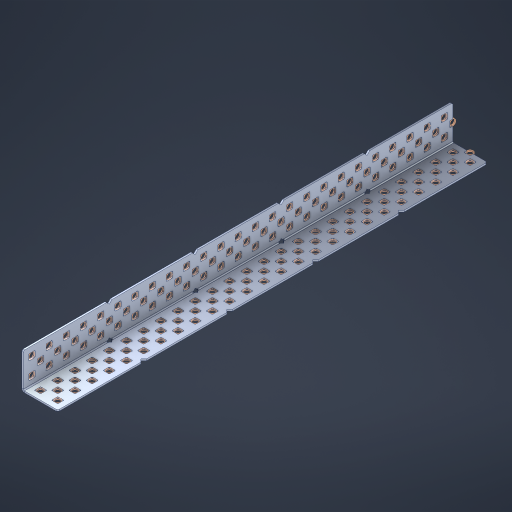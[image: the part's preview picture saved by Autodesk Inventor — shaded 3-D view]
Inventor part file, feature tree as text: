
AUTODESK INVENTOR PART (.ipt)
format: ipt  version: 2023 (Build 270158000, 158)  size: 1,781,248 bytes
history: native  units: in
note: dims shown in document units (in); Inventor stores cm internally (conversion verified against a paired STEP export)
features: other x156, extrude x148, sheet_metal_op x8, sketch x7, pattern_linear x2, mirror x1, chamfer x1
ambient origin geometry x8: Origin, YZ Plane, XZ Plane, XY Plane, X Axis, Y Axis, Z Axis, Center Point
bodies: Solid1 (feature_tree), Body (feature_tree)
feature tree (323):
  sheet_metal_op  "Flanges"
  sheet_metal_op  "Body Pattern"
  pattern_linear  "Center Pattern"  Spacing1=1.0in  [1 undecoded]
  other  "Arc Length"
  pattern_linear  "Notch Pattern"  Spacing1=0.1875in  [1 undecoded]
  other  "Diagonal Plane"
  mirror  "Everything Mirrored"
  chamfer  "End Chamfer"
  sketch  "Sketch1"  dims[d0=1.0in]
  other  "Plate1"
  sketch  "Sketch2"  dims[d1=12.5in]
  other  "Plate2"
  sheet_metal_op  "Bend1"
  sheet_metal_op  "Corner1"
  sketch  "Sketch8"  dims[d2=0.0469in]
  sketch  "Sketch9"  dims[d3=0.0469in]
  other  "Srf91"
  sheet_metal_op  "Body Pattern Sketch"
  other  "Srf92"
  sketch  "Sketch13"  dims[d4=0.0234in]
  sketch  "Sketch15"  dims[d5=0.0938in]
  sketch  "Sketch16"  dims[d6=0.0469in d7=1.0in d8=90.0deg d9=0.0312in d10=0.1875in d11=0.0469in d12=0.0469in d49=0.182in d50=0.02in d52=0.25in d53=0.0469in d54=0.0in d55=0.172in d56=1.0in d57=0.0in d60=9.8425in d62=0.5in d63=0.7874in d65=0.5in d85=0.1473in d86=0.1659in d89=0.0469in d90=0.0in d91=0.04in d92=0.0491in d95=2.5in d96=0.04in d97=0.25in d98=45.0deg d99=0.25in d106=0.182in d107=0.02in d108=0.5in d110=0.0469in d111=0.0in d112=0.172in d113=0.5in d114=0.0in d117=0.5in d123=0.25in d125=0.25in d126=0.0491in d127=0.1227in d128=0.08in d129=0.04in d130=2.5in]
  other  "Srf786"
  other  "Srf856"
  other  "Srf857"
  other  "Srf858"
  other  "Srf859"
  other  "Srf860"
  other  "Srf861"
  other  "Srf889"
  other  "Srf890"
  other  "Srf891"
  other  "Srf1275"
  other  "Srf1276"
  other  "Srf1278"
  other  "Srf1279"
  other  "Srf1280"
  other  "Srf1281"
  other  "Srf1282"
  other  "Srf1283"
  other  "Srf1277"
  other  "Srf1285"
  other  "Srf1286"
  other  "Srf1287"
  other  "Srf1383"
  other  "Srf1384"
  other  "Srf1385"
  other  "Srf1386"
  other  "Srf1387"
  other  "Srf1388"
  other  "Srf1389"
  other  "Srf1390"
  other  "Srf1391"
  other  "Srf1392"
  other  "Srf1393"
  other  "Srf1394"
  other  "Srf1395"
  other  "Srf1396"
  other  "Srf1397"
  other  "Srf1398"
  other  "Srf1399"
  other  "Srf1400"
  other  "Srf1401"
  other  "Srf1402"
  other  "Srf1403"
  other  "Srf1404"
  other  "Srf1405"
  other  "Srf1406"
  other  "Srf1407"
  other  "Srf1408"
  other  "Srf1409"
  other  "Srf1410"
  other  "Srf1411"
  other  "Srf1412"
  other  "Srf1413"
  other  "Srf1414"
  other  "Srf1415"
  other  "Srf1416"
  other  "Srf1417"
  other  "Srf1418"
  other  "Srf1419"
  other  "Srf1420"
  other  "Srf1421"
  other  "Srf1422"
  other  "Srf1423"
  other  "Srf1424"
  other  "Srf1445"
  other  "Srf1446"
  other  "Srf1447"
  other  "Srf1448"
  other  "Srf1449"
  other  "Srf1450"
  other  "Srf1451"
  other  "Srf1452"
  other  "Srf1453"
  other  "Srf1454"
  other  "Srf1455"
  other  "Srf1456"
  other  "Srf1457"
  other  "Srf1458"
  other  "Srf1459"
  other  "Srf1460"
  other  "Srf1461"
  other  "Srf1462"
  other  "Srf1463"
  other  "Srf1464"
  other  "Srf1465"
  other  "Srf1475"
  other  "Srf1476"
  other  "Srf1477"
  other  "Srf1478"
  other  "Srf1479"
  other  "Srf1480"
  other  "Srf1481"
  other  "Srf1482"
  other  "Srf1483"
  other  "Srf1484"
  other  "Srf1485"
  other  "Srf1486"
  other  "Srf1487"
  other  "Srf1488"
  other  "Srf1489"
  other  "Srf1490"
  other  "Srf1491"
  other  "Srf1492"
  other  "Srf1493"
  other  "Srf1494"
  other  "Srf1495"
  other  "Srf1496"
  other  "Srf1497"
  other  "Srf1498"
  other  "Srf1499"
  other  "Srf1500"
  other  "Srf1501"
  other  "Srf1502"
  other  "Srf1503"
  other  "Srf1504"
  other  "Srf1505"
  other  "Srf1506"
  other  "Srf1507"
  other  "Srf1508"
  other  "Srf1509"
  other  "Srf1510"
  other  "Srf1511"
  other  "Srf1512"
  other  "Srf1513"
  other  "Srf1514"
  other  "Srf1515"
  other  "Srf1516"
  other  "Srf1537"
  other  "Srf1538"
  other  "Srf1539"
  other  "Srf1540"
  other  "Srf1541"
  other  "Srf1542"
  other  "Srf1543"
  other  "Srf1544"
  other  "Srf1545"
  other  "Srf1546"
  other  "Srf1547"
  other  "Srf1548"
  other  "Srf1549"
  other  "Srf1550"
  other  "Srf1551"
  other  "Srf1552"
  other  "Srf1553"
  other  "Srf1554"
  other  "Srf1555"
  other  "Srf1556"
  other  "Srf1557"
  sheet_metal_op  "Body Stamp"
  sheet_metal_op  "Body Circle"
  other  "Center Stamp"
  other  "Center Circle"
  sheet_metal_op  "Notch"
  extrude  "ExtrusionSrf92"  Depth=0.0469in
  extrude  "ExtrusionSrf856"  Depth=0.0469in
  extrude  "ExtrusionSrf857"  Depth=0.182in
  extrude  "ExtrusionSrf858"  Depth=0.02in
  extrude  "ExtrusionSrf859"  Depth=0.25in
  extrude  "ExtrusionSrf860"  Depth=0.0469in
  extrude  "ExtrusionSrf861"  TaperAngle=0.0deg  [1 undecoded]
  extrude  "ExtrusionSrf889"  Depth=2.5in
  extrude  "ExtrusionSrf890"  Depth=1.0in TaperAngle=0.0deg
  extrude  "ExtrusionSrf891"  Depth=2.5in
  extrude  "ExtrusionSrf1275"  Depth=0.5in
  extrude  "ExtrusionSrf1276"  Depth=2.5in
  extrude  "ExtrusionSrf1277"  Depth=2.5in
  extrude  "ExtrusionSrf1278"  Depth=0.0469in
  extrude  "ExtrusionSrf1279"  Depth=2.5in TaperAngle=0.0deg
  extrude  "ExtrusionSrf1280"  Depth=2.5in
  extrude  "ExtrusionSrf1281"  Depth=0.25in TaperAngle=45.0deg
  extrude  "ExtrusionSrf1282"  Depth=0.25in
  extrude  "ExtrusionSrf1345"  Depth=0.182in
  extrude  "ExtrusionSrf1346"  Depth=0.02in
  extrude  "ExtrusionSrf1347"  Depth=0.5in
  extrude  "ExtrusionSrf1348"  Depth=0.0469in
  extrude  "ExtrusionSrf1383"  TaperAngle=0.0deg  [1 undecoded]
  extrude  "ExtrusionSrf1384"  Depth=2.5in
  extrude  "ExtrusionSrf1385"  Depth=0.5in TaperAngle=0.0deg
  extrude  "ExtrusionSrf1386"  Depth=0.5in
  extrude  "ExtrusionSrf1387"  Depth=0.25in
  extrude  "ExtrusionSrf1388"  Depth=0.25in
  extrude  "ExtrusionSrf1389"  Depth=2.5in
  extrude  "ExtrusionSrf1390"  Depth=2.5in
  extrude  "ExtrusionSrf1391"  Depth=2.5in
  extrude  "ExtrusionSrf1392"  Depth=2.5in
  extrude  "ExtrusionSrf1393"  Depth=2.5in
  extrude  "ExtrusionSrf1394"  [1 undecoded]
  extrude  "ExtrusionSrf1395"  [1 undecoded]
  extrude  "ExtrusionSrf1396"  [1 undecoded]
  extrude  "ExtrusionSrf1397"  [1 undecoded]
  extrude  "ExtrusionSrf1398"  [1 undecoded]
  extrude  "ExtrusionSrf1399"  [1 undecoded]
  extrude  "ExtrusionSrf1400"  [1 undecoded]
  extrude  "ExtrusionSrf1401"  [1 undecoded]
  extrude  "ExtrusionSrf1402"  [1 undecoded]
  extrude  "ExtrusionSrf1403"  [1 undecoded]
  extrude  "ExtrusionSrf1404"  [1 undecoded]
  extrude  "ExtrusionSrf1405"  [1 undecoded]
  extrude  "ExtrusionSrf1406"  [1 undecoded]
  extrude  "ExtrusionSrf1407"  [1 undecoded]
  extrude  "ExtrusionSrf1408"  [1 undecoded]
  extrude  "ExtrusionSrf1409"  [1 undecoded]
  extrude  "ExtrusionSrf1410"  [1 undecoded]
  extrude  "ExtrusionSrf1411"  [1 undecoded]
  extrude  "ExtrusionSrf1412"  [1 undecoded]
  extrude  "ExtrusionSrf1413"  [1 undecoded]
  extrude  "ExtrusionSrf1414"  [1 undecoded]
  extrude  "ExtrusionSrf1415"  [1 undecoded]
  extrude  "ExtrusionSrf1416"  [1 undecoded]
  extrude  "ExtrusionSrf1417"  [1 undecoded]
  extrude  "ExtrusionSrf1418"  [1 undecoded]
  extrude  "ExtrusionSrf1419"  [1 undecoded]
  extrude  "ExtrusionSrf1420"  [1 undecoded]
  extrude  "ExtrusionSrf1421"  [1 undecoded]
  extrude  "ExtrusionSrf1422"  [1 undecoded]
  extrude  "ExtrusionSrf1423"  [1 undecoded]
  extrude  "ExtrusionSrf1424"  [1 undecoded]
  extrude  "ExtrusionSrf1445"  [1 undecoded]
  extrude  "ExtrusionSrf1446"  [1 undecoded]
  extrude  "ExtrusionSrf1447"  [1 undecoded]
  extrude  "ExtrusionSrf1448"  [1 undecoded]
  extrude  "ExtrusionSrf1449"  [1 undecoded]
  extrude  "ExtrusionSrf1450"  [1 undecoded]
  extrude  "ExtrusionSrf1451"  [1 undecoded]
  extrude  "ExtrusionSrf1452"  [1 undecoded]
  extrude  "ExtrusionSrf1453"  [1 undecoded]
  extrude  "ExtrusionSrf1454"  [1 undecoded]
  extrude  "ExtrusionSrf1455"  [1 undecoded]
  extrude  "ExtrusionSrf1456"  [1 undecoded]
  extrude  "ExtrusionSrf1457"  [1 undecoded]
  extrude  "ExtrusionSrf1458"  [1 undecoded]
  extrude  "ExtrusionSrf1459"  [1 undecoded]
  extrude  "ExtrusionSrf1460"  [1 undecoded]
  extrude  "ExtrusionSrf1461"  [1 undecoded]
  extrude  "ExtrusionSrf1462"  [1 undecoded]
  extrude  "ExtrusionSrf1463"  [1 undecoded]
  extrude  "ExtrusionSrf1464"  [1 undecoded]
  extrude  "ExtrusionSrf1465"  [1 undecoded]
  extrude  "ExtrusionSrf1475"  [1 undecoded]
  extrude  "ExtrusionSrf1476"  [1 undecoded]
  extrude  "ExtrusionSrf1477"  [1 undecoded]
  extrude  "ExtrusionSrf1478"  [1 undecoded]
  extrude  "ExtrusionSrf1479"  [1 undecoded]
  extrude  "ExtrusionSrf1480"  [1 undecoded]
  extrude  "ExtrusionSrf1481"  [1 undecoded]
  extrude  "ExtrusionSrf1482"  [1 undecoded]
  extrude  "ExtrusionSrf1483"  [1 undecoded]
  extrude  "ExtrusionSrf1484"  [1 undecoded]
  extrude  "ExtrusionSrf1485"  [1 undecoded]
  extrude  "ExtrusionSrf1486"  [1 undecoded]
  extrude  "ExtrusionSrf1487"  [1 undecoded]
  extrude  "ExtrusionSrf1488"  [1 undecoded]
  extrude  "ExtrusionSrf1489"  [1 undecoded]
  extrude  "ExtrusionSrf1490"  [1 undecoded]
  extrude  "ExtrusionSrf1491"  [1 undecoded]
  extrude  "ExtrusionSrf1492"  [1 undecoded]
  extrude  "ExtrusionSrf1493"  [1 undecoded]
  extrude  "ExtrusionSrf1494"  [1 undecoded]
  extrude  "ExtrusionSrf1495"  [1 undecoded]
  extrude  "ExtrusionSrf1496"  [1 undecoded]
  extrude  "ExtrusionSrf1497"  [1 undecoded]
  extrude  "ExtrusionSrf1498"  [1 undecoded]
  extrude  "ExtrusionSrf1499"  [1 undecoded]
  extrude  "ExtrusionSrf1500"  [1 undecoded]
  extrude  "ExtrusionSrf1501"  [1 undecoded]
  extrude  "ExtrusionSrf1502"  [1 undecoded]
  extrude  "ExtrusionSrf1503"  [1 undecoded]
  extrude  "ExtrusionSrf1504"  [1 undecoded]
  extrude  "ExtrusionSrf1505"  [1 undecoded]
  extrude  "ExtrusionSrf1506"  [1 undecoded]
  extrude  "ExtrusionSrf1507"  [1 undecoded]
  extrude  "ExtrusionSrf1508"  [1 undecoded]
  extrude  "ExtrusionSrf1509"  [1 undecoded]
  extrude  "ExtrusionSrf1510"  [1 undecoded]
  extrude  "ExtrusionSrf1511"  [1 undecoded]
  extrude  "ExtrusionSrf1512"  [1 undecoded]
  extrude  "ExtrusionSrf1513"  [1 undecoded]
  extrude  "ExtrusionSrf1514"  [1 undecoded]
  extrude  "ExtrusionSrf1515"  [1 undecoded]
  extrude  "ExtrusionSrf1516"  [1 undecoded]
  extrude  "ExtrusionSrf1537"  [1 undecoded]
  extrude  "ExtrusionSrf1538"  [1 undecoded]
  extrude  "ExtrusionSrf1539"  [1 undecoded]
  extrude  "ExtrusionSrf1540"  [1 undecoded]
  extrude  "ExtrusionSrf1541"  [1 undecoded]
  extrude  "ExtrusionSrf1542"  [1 undecoded]
  extrude  "ExtrusionSrf1543"  [1 undecoded]
  extrude  "ExtrusionSrf1544"  [1 undecoded]
  extrude  "ExtrusionSrf1545"  [1 undecoded]
  extrude  "ExtrusionSrf1546"  [1 undecoded]
  extrude  "ExtrusionSrf1547"  [1 undecoded]
  extrude  "ExtrusionSrf1548"  [1 undecoded]
  extrude  "ExtrusionSrf1549"  [1 undecoded]
  extrude  "ExtrusionSrf1550"  [1 undecoded]
  extrude  "ExtrusionSrf1551"  [1 undecoded]
  extrude  "ExtrusionSrf1552"  [1 undecoded]
  extrude  "ExtrusionSrf1553"  [1 undecoded]
  extrude  "ExtrusionSrf1554"  [1 undecoded]
  extrude  "ExtrusionSrf1555"  [1 undecoded]
  extrude  "ExtrusionSrf1556"  [1 undecoded]
  extrude  "ExtrusionSrf1557"  [1 undecoded]
note: 119 required parameter values undecoded (feature->parameter linkage not recoverable at this tier; creation-order binding heuristic only, values carry confidence <= 0.55)
